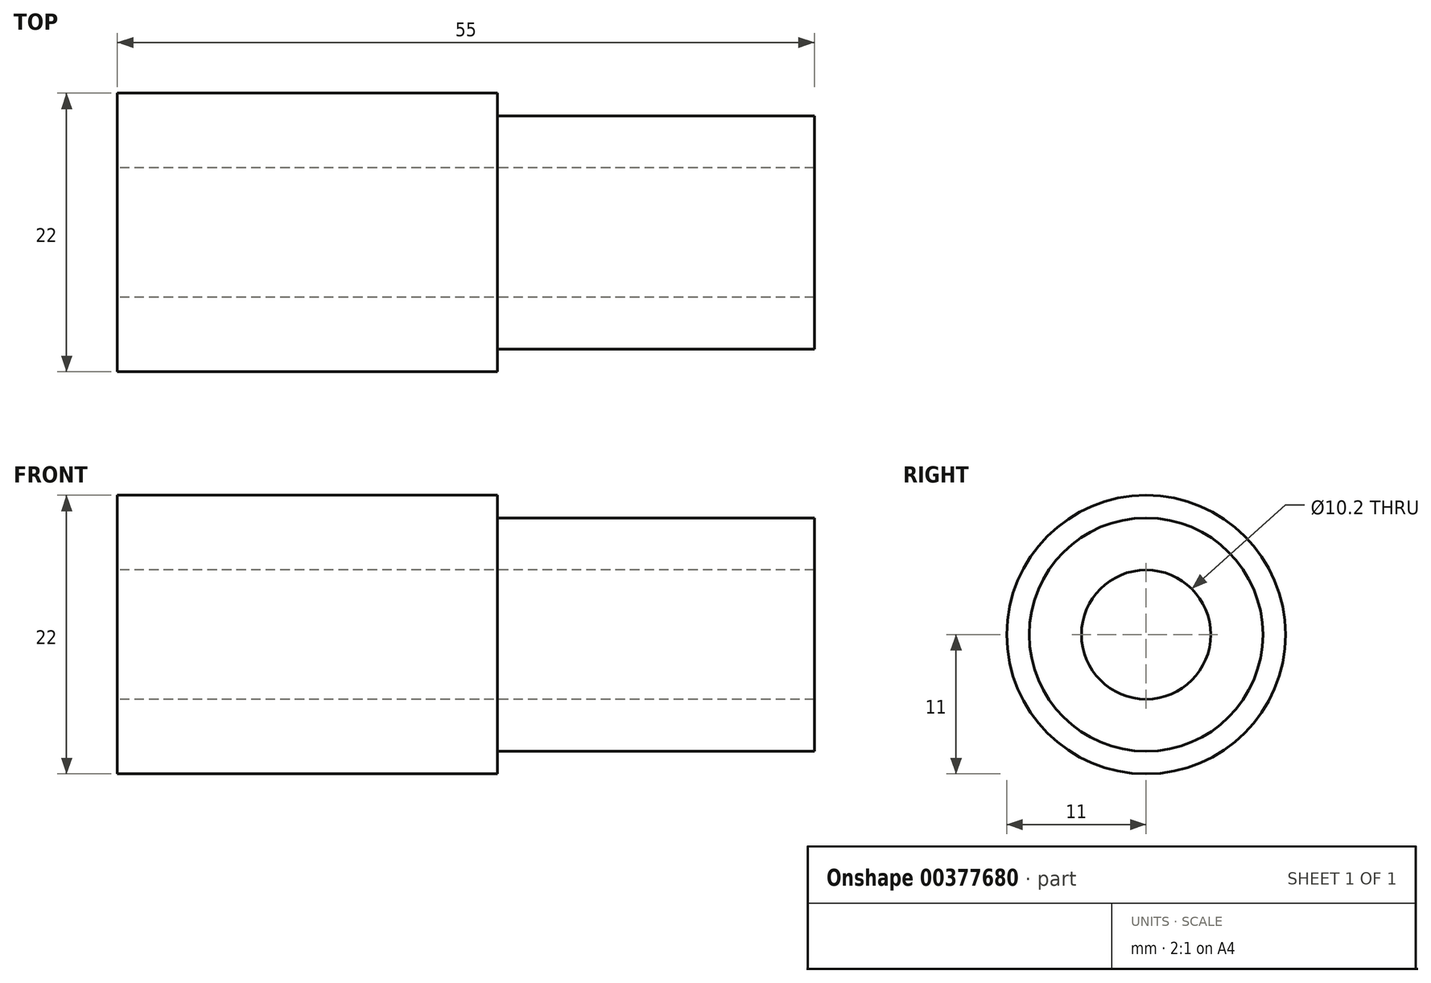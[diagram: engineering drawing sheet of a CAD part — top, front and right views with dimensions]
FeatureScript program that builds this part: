
annotation { "Feature Type Name" : "Feature", "Feature Type Description" : "" }
export const myFeature = defineFeature(function(context is Context, id is Id, definition is map)
    precondition{}
    {
        {
            var Q0;
            Q0=qCreatedBy(makeId("Right.planeOp"),FACE);
            var sketch = newSketch(context, id + "F0", { "sketchPlane" : qUnion([Q0])});
            skCircle(sketch, "E0", {"center": v(0, 0) * mm, "radius": 11 * mm});
            skCircle(sketch, "E1", {"center": v(0, 0) * mm, "radius": 5.1 * mm});
            skSolve(sketch);
        }
        {
            var Q0;
            Q0 = qSketchRegion(id + "F0", true);
            extrude(context, id + "F1", {"entities" : qUnion([Q0]), "depth" : 55 * mm});
        }
        {
            var Q0;
            Q0=makeQuery(id+"F1.opExtrude","CAP_FACE",FACE,{"disambiguationData":[OSD([sQuery(id+"F0.wireOp",EDGE,"E0"),sQuery(id+"F0.wireOp",EDGE,"E1")])],"isStart":false});
            var sketch = newSketch(context, id + "F2", { "sketchPlane" : qUnion([Q0])});
            skCircle(sketch, "E2", {"center": v(0, 0) * mm, "radius": 9.22 * mm});
            skCircle(sketch, "E3", {"center": v(0, 0) * mm, "radius": 12.84 * mm});
            skSolve(sketch);
        }
        {
            var Q0;
            Q0 = qSketchRegion(id + "F2", true);
            extrude(context, id + "F3", {"entities" : qUnion([Q0]), "operationType" : NewBodyOperationType.REMOVE, "oppositeDirection" : true, "depth" : 25 * mm});
        }
    });
